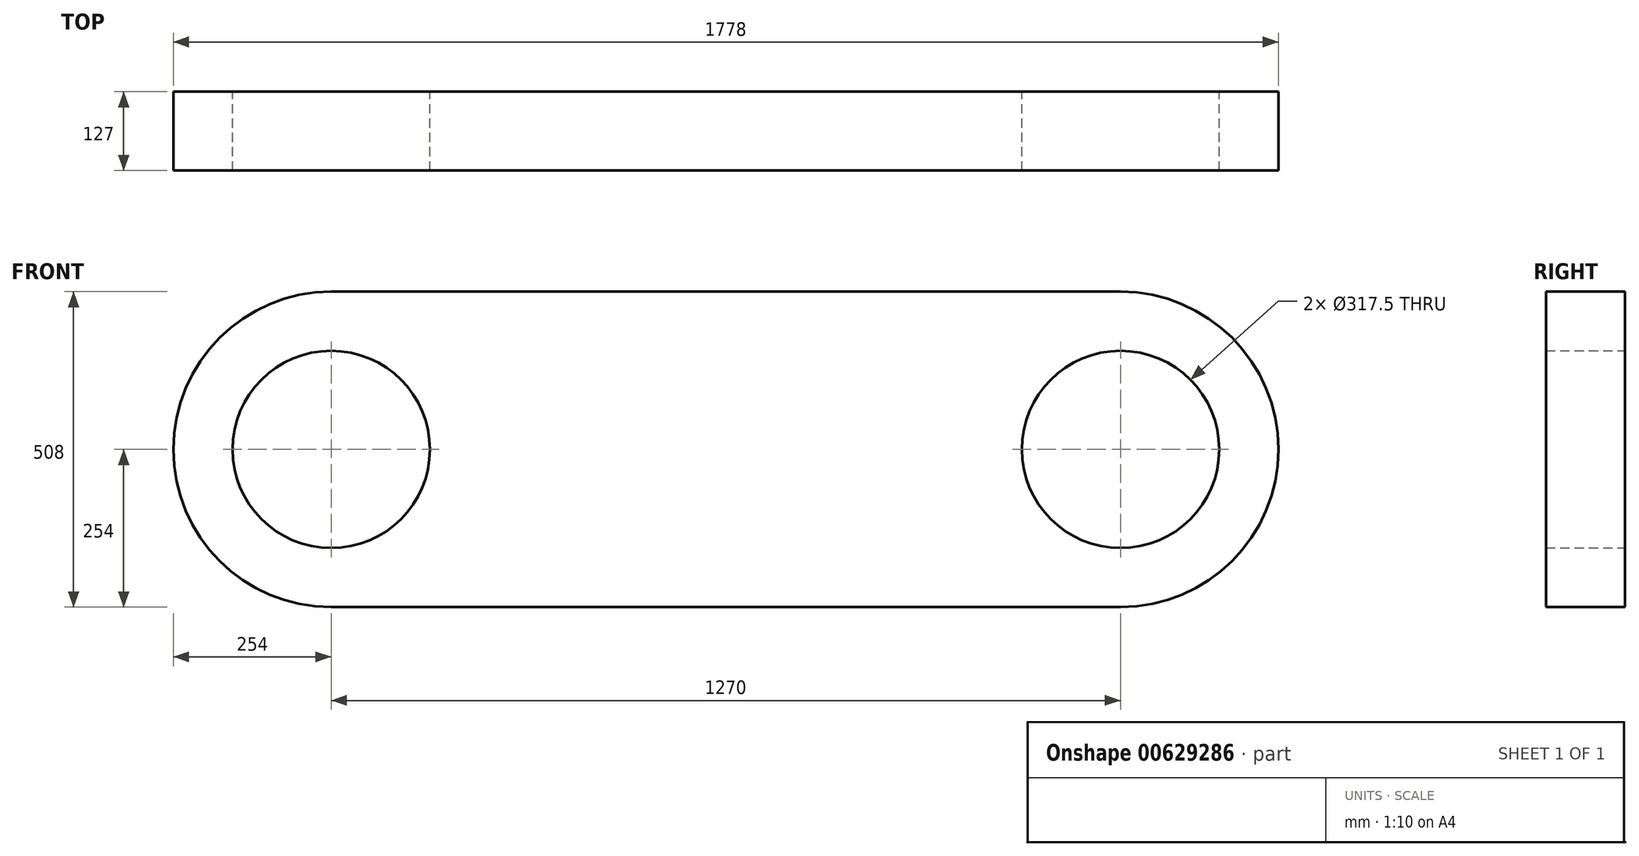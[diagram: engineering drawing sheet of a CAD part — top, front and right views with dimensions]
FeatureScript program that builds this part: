
annotation { "Feature Type Name" : "Feature", "Feature Type Description" : "" }
export const myFeature = defineFeature(function(context is Context, id is Id, definition is map)
    precondition{}
    {
        {
            var Q0;
            Q0=qCreatedBy(makeId("Front.planeOp"),FACE);
            var sketch = newSketch(context, id + "F0", { "sketchPlane" : qUnion([Q0])});
            skLineSegment(sketch, "E0.bottom", {"start": v(-635, 254) * mm, "end": v(635, 254) * mm});
            skLineSegment(sketch, "E0.top", {"start": v(-635, -254) * mm, "end": v(635, -254) * mm});
            skArc(sketch, "E1", {"start": v(635, -254) * mm, "mid": v(889, 0) * mm, "end": v(635, 254) * mm});
            skArc(sketch, "E2", {"start": v(-635, 254) * mm, "mid": v(-889, 0) * mm, "end": v(-635, -254) * mm});
            skCircle(sketch, "E3", {"center": v(-635, 0) * mm, "radius": 158.75 * mm});
            skCircle(sketch, "E4", {"center": v(635, 0) * mm, "radius": 158.75 * mm});
            skSolve(sketch);
        }
        {
            var Q0;
            Q0 = qSketchRegion(id + "F0", true);
            extrude(context, id + "F1", {"entities" : qUnion([Q0]), "depth" : 127 * mm, "offsetDistance" : 25.4 * mm});
        }
    });
